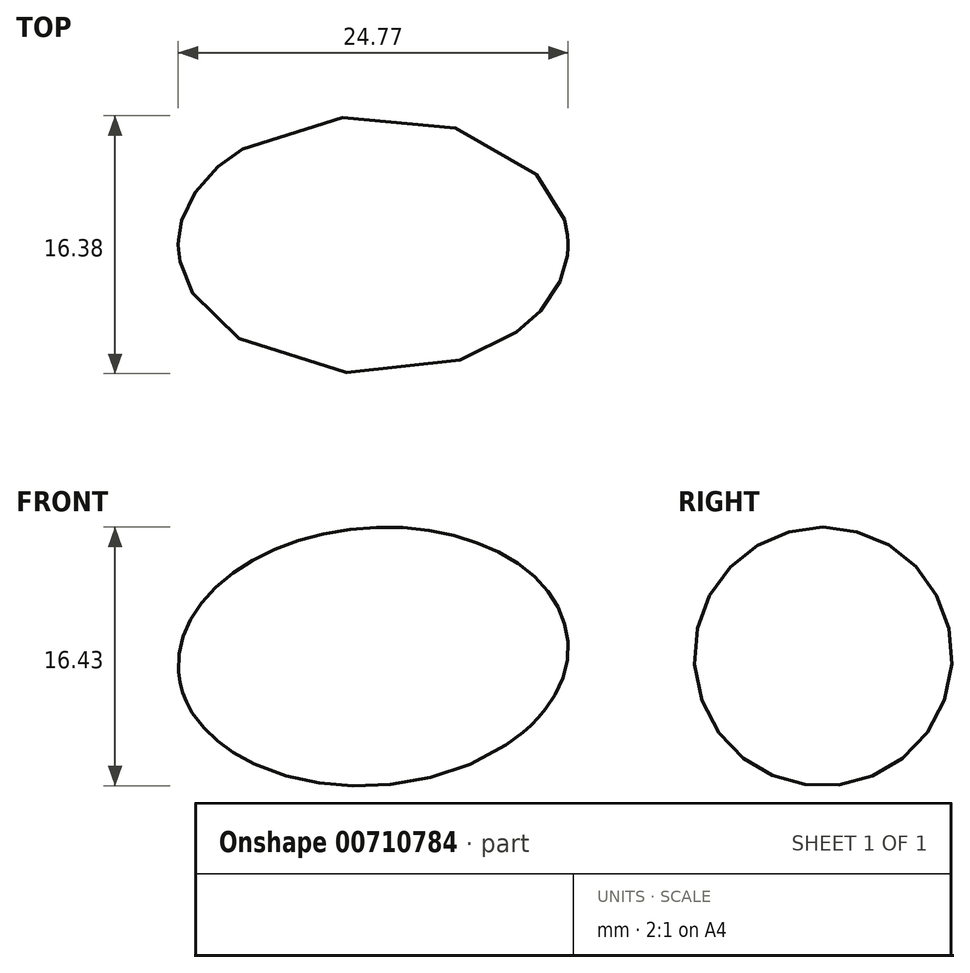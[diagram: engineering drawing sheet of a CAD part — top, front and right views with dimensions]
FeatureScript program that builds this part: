
annotation { "Feature Type Name" : "Feature", "Feature Type Description" : "" }
export const myFeature = defineFeature(function(context is Context, id is Id, definition is map)
    precondition{}
    {
        {
            var Q0;
            Q0=qCreatedBy(makeId("Front.planeOp"),FACE);
            var sketch = newSketch(context, id + "F0", { "sketchPlane" : qUnion([Q0])});
            skLineSegment(sketch, "E0", {"start": v(14.87, 82.66) * mm, "end": v(39.6, 84.6) * mm});
            skEllipse(sketch, "E1", {"center": v(27.23, 83.63) * mm, "majorRadius": 12.4 * mm, "minorRadius": 8.19 * mm, "majorAxis": v(1, 0.08)});
            skLineSegment(sketch, "E2", {"start": v(28.35, 100.13) * mm, "end": v(1.86, 96.16) * mm, "construction": true});
            skEllipse(sketch, "E3", {"center": v(15.1, 98.14) * mm, "majorRadius": 13.39 * mm, "minorRadius": 11.4 * mm, "majorAxis": v(-0.99, -0.15), "construction": true});
            skLineSegment(sketch, "E4", {"start": v(1.76, 83.48) * mm, "end": v(1.76, 111.73) * mm, "construction": true});
            skPoint(sketch, "E5", {"position": v(1.76, 97.6) * mm});
            skLineSegment(sketch, "E6", {"start": v(28.45, 109.08) * mm, "end": v(28.45, 88.3) * mm, "construction": true});
            skPoint(sketch, "E7", {"position": v(28.45, 98.68) * mm});
            skFitSpline(sketch, "E8", {"points": [v(-22.54, -44.4) * mm, v(-35.9, 56.36) * mm, v(-22.75, 97.53) * mm, v(3.02, 107.39) * mm], "startDerivative": vector(-46.6, 229.03) * mm, "endDerivative": vector(129.4, 68.8) * mm});
            skFitSpline(sketch, "E9", {"points": [v(-7.27, 95.4) * mm, v(8.98, 108.06) * mm], "startDerivative": vector(10.4, 17.14) * mm, "endDerivative": vector(34.28, 2.3) * mm});
            skFitSpline(sketch, "E10", {"points": [v(58.34, -44.4) * mm, v(55.92, -3.94) * mm, v(47.67, 34.1) * mm, v(36.88, 61.1) * mm], "startDerivative": vector(-1.45, 94.2) * mm, "endDerivative": vector(-40.32, 116.17) * mm});
            skFitSpline(sketch, "E11", {"points": [v(14.67, -39.53) * mm, v(64.22, -28.63) * mm, v(69.96, -44.4) * mm], "startDerivative": vector(50.75, 22.5) * mm, "endDerivative": vector(4.35, -54.22) * mm});
            skFitSpline(sketch, "E12", {"points": [v(13.3, -32.28) * mm, v(25.87, -3.06) * mm, v(22.4, 19.45) * mm, v(27.64, 34) * mm, v(29.44, 54.05) * mm, v(27.87, 75.47) * mm], "startDerivative": vector(76.8, 122.37) * mm, "endDerivative": vector(-136.15, 46.1) * mm});
            skFitSpline(sketch, "E13", {"points": [v(10.6, 78.2) * mm, v(3.5, 66.51) * mm, v(7.2, 43.67) * mm, v(17.25, 58.63) * mm, v(27.52, 71.43) * mm], "startDerivative": vector(-41.18, -37.41) * mm, "endDerivative": vector(42.38, 41.81) * mm});
            skFitSpline(sketch, "E14", {"points": [v(-1.84, 75.23) * mm, v(8.71, 72.57) * mm, v(20.8, 74.9) * mm], "startDerivative": vector(21.36, -7.92) * mm, "endDerivative": vector(23.89, 7.08) * mm});
            skFitSpline(sketch, "E15", {"points": [v(33.84, 62.55) * mm, v(32.39, 75.18) * mm], "startDerivative": vector(7.17, 13.73) * mm, "endDerivative": vector(-14.66, 5.88) * mm});
            skSolve(sketch);
        }
        {
            var Q0;
            {var subQ0=sQuery(id+"F0.wireOp",EDGE,"E0");Q0=makeQuery(id+"F0.imprint","IMPRINT",FACE,{"disambiguationData":[TD([[makeQuery(id+"F0.imprint","IMPRINT",EDGE,{"derivedFrom":subQ0}),1.0]])]});}
            var Q1;
            Q1=sQuery(id+"F0.wireOp",EDGE,"E0");
            revolve(context, id + "F1", {"surfaceOperationType" : NewSurfaceOperationType.NEW, "entities" : qUnion([Q0]), "axis" : qUnion([Q1]), "revolveType" : RevolveType.FULL});
        }
    });
